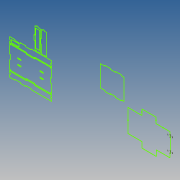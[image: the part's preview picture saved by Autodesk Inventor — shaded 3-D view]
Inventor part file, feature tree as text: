
AUTODESK INVENTOR PART (.ipt)
format: ipt  version: 2020 (Build 240168000, 168)  size: 140,800 bytes
history: native  units: mm
features: sketch x1
ambient origin geometry x8: Origin, YZ Plane, XZ Plane, XY Plane, X Axis, Y Axis, Z Axis, Center Point
feature tree (1):
  sketch  "Sketch1"  dims[d268=3.0mm d269=3.0mm]
